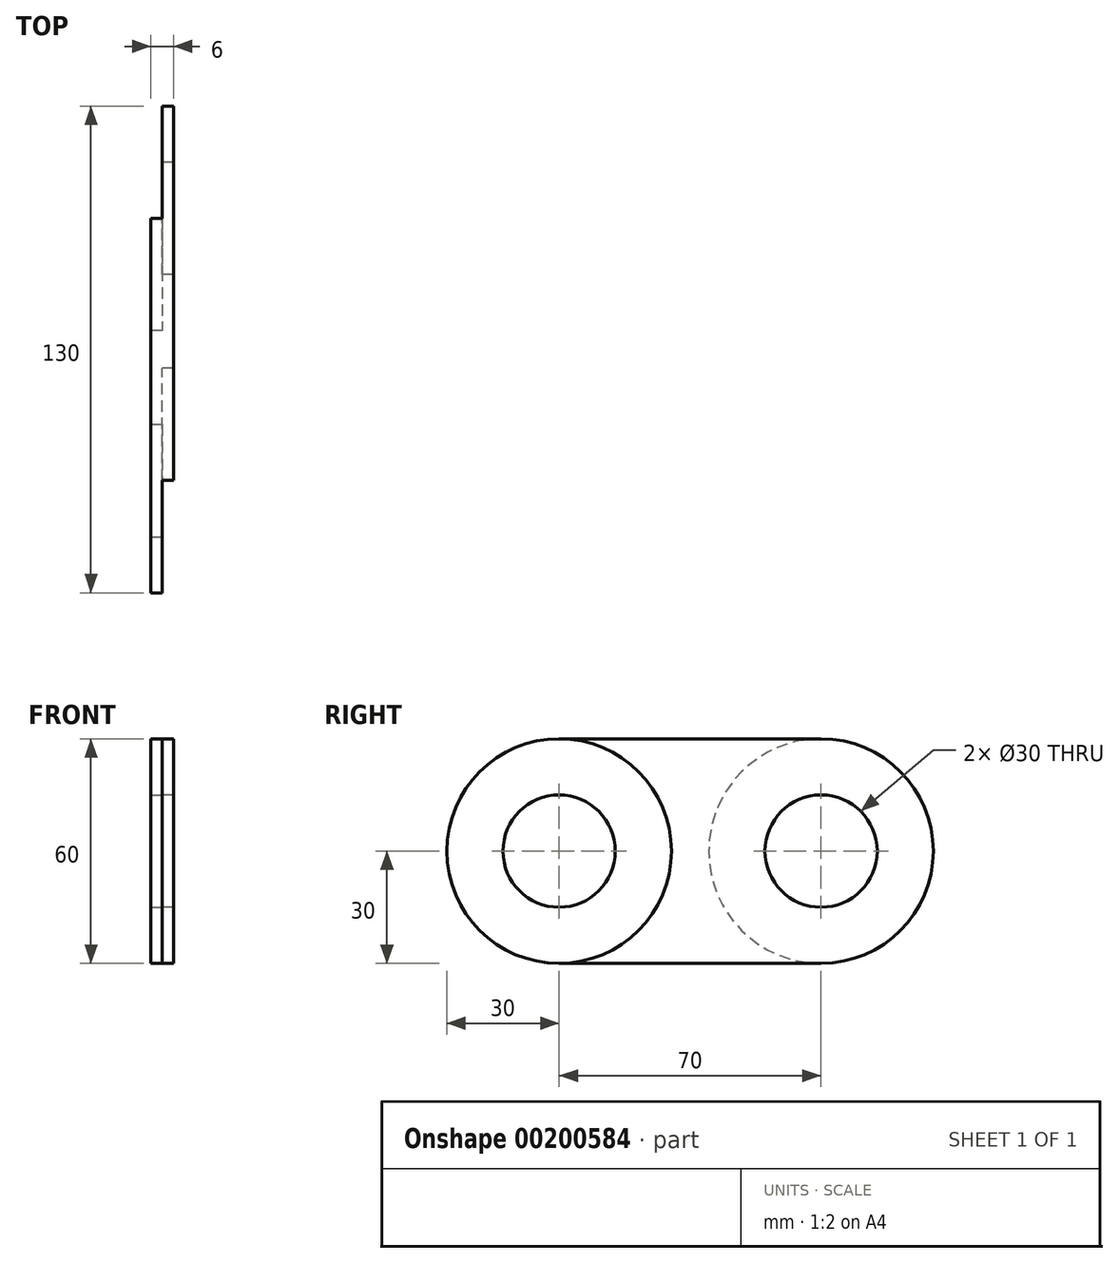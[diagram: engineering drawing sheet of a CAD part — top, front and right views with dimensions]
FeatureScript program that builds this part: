
annotation { "Feature Type Name" : "Feature", "Feature Type Description" : "" }
export const myFeature = defineFeature(function(context is Context, id is Id, definition is map)
    precondition{}
    {
        {
            var Q0;
            Q0=qCreatedBy(makeId("Right.planeOp"),FACE);
            var sketch = newSketch(context, id + "F0", { "sketchPlane" : qUnion([Q0])});
            skCircle(sketch, "E0", {"center": v(-70, 0) * mm, "radius": 30 * mm});
            skCircle(sketch, "E1", {"center": v(0, 0) * mm, "radius": 30 * mm});
            skLineSegment(sketch, "E2", {"start": v(-70, 30) * mm, "end": v(0, 30) * mm});
            skLineSegment(sketch, "E3", {"start": v(-70, -30) * mm, "end": v(0, -30) * mm});
            skCircle(sketch, "E4", {"center": v(0, 0) * mm, "radius": 15 * mm});
            skCircle(sketch, "E5", {"center": v(-70, 0) * mm, "radius": 15 * mm});
            skSolve(sketch);
        }
        {
            var Q0;
            {var subQ0=sQuery(id+"F0.wireOp",EDGE,"E2");Q0=makeQuery(id+"F0.imprint","IMPRINT",FACE,{"disambiguationData":[TD([[makeQuery(id+"F0.imprint","IMPRINT",EDGE,{"derivedFrom":subQ0}),-1.0]])]});}
            extrude(context, id + "F1", {"entities" : qUnion([Q0]), "depth" : 3 * mm, "hasSecondDirection" : true, "secondDirectionOppositeDirection" : true, "secondDirectionDepth" : 3 * mm});
        }
        {
            var Q0;
            Q0=makeQuery(id+"F0.imprint","IMPRINT",FACE,{"disambiguationData":[TD([[makeQuery(id+"F0.imprint","IMPRINT",EDGE,{"derivedFrom":sQuery(id+"F0.wireOp",EDGE,"E4")}),-1.0]])]});
            extrude(context, id + "F2", {"entities" : qUnion([Q0]), "operationType" : NewBodyOperationType.ADD, "depth" : 3 * mm});
        }
        {
            var Q0;
            Q0=makeQuery(id+"F0.imprint","IMPRINT",FACE,{"disambiguationData":[TD([[makeQuery(id+"F0.imprint","IMPRINT",EDGE,{"derivedFrom":sQuery(id+"F0.wireOp",EDGE,"E5")}),-1.0]])]});
            extrude(context, id + "F3", {"entities" : qUnion([Q0]), "operationType" : NewBodyOperationType.ADD, "oppositeDirection" : true, "depth" : 3 * mm});
        }
    });
